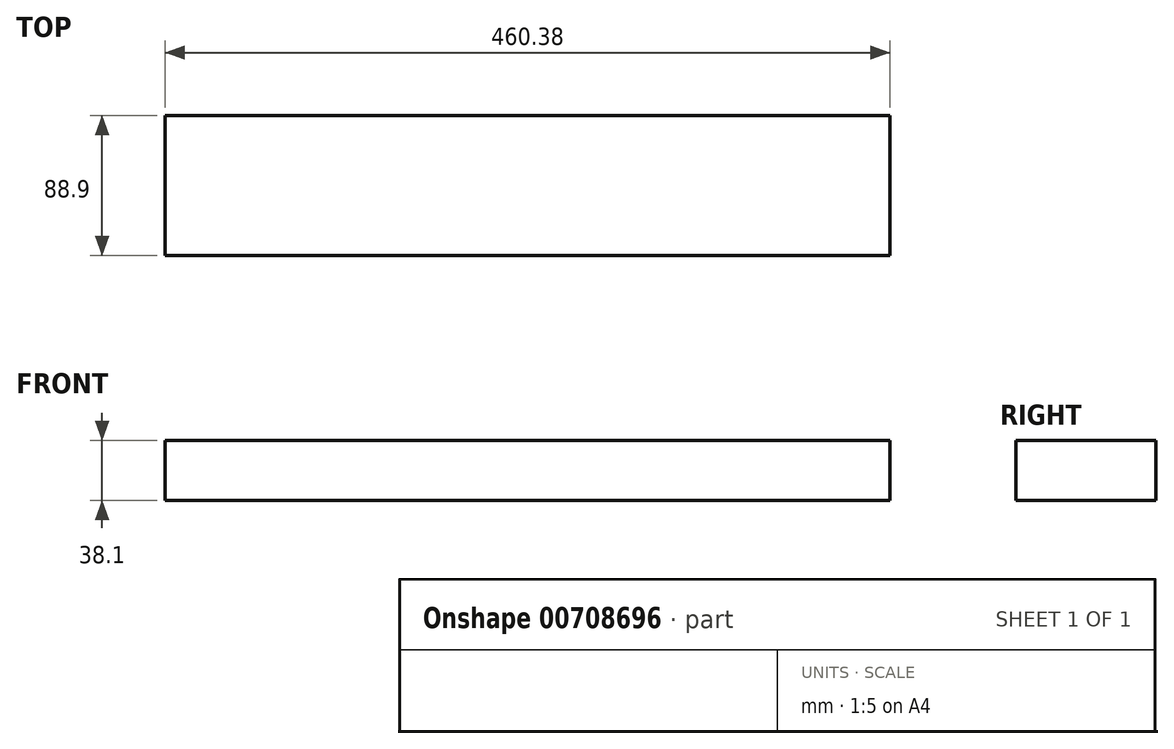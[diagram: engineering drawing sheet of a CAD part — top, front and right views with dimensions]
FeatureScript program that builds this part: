
annotation { "Feature Type Name" : "Feature", "Feature Type Description" : "" }
export const myFeature = defineFeature(function(context is Context, id is Id, definition is map)
    precondition{}
    {
        {
            var Q0;
            Q0=qCreatedBy(makeId("Right.planeOp"),FACE);
            var sketch = newSketch(context, id + "F0", { "sketchPlane" : qUnion([Q0])});
            skLineSegment(sketch, "E0.bottom", {"start": v(44.45, 19.05) * mm, "end": v(-44.45, 19.05) * mm});
            skLineSegment(sketch, "E0.top", {"start": v(44.45, -19.05) * mm, "end": v(-44.45, -19.05) * mm});
            skLineSegment(sketch, "E0.left", {"start": v(44.45, 19.05) * mm, "end": v(44.45, -19.05) * mm});
            skLineSegment(sketch, "E0.right", {"start": v(-44.45, 19.05) * mm, "end": v(-44.45, -19.05) * mm});
            skPoint(sketch, "E0.middle", {"position": v(0, 0) * mm});
            skSolve(sketch);
        }
        {
            var Q0;
            Q0=makeQuery(id+"F0.imprint","IMPRINT",FACE,{"disambiguationData":[TD([[makeQuery(id+"F0.imprint","IMPRINT",EDGE,{"derivedFrom":sQuery(id+"F0.wireOp",EDGE,"E0.bottom")}),1.0]])]});
            extrude(context, id + "F1", {"entities" : qUnion([Q0]), "endBound" : BoundingType.SYMMETRIC, "depth" : 460.38 * mm, "offsetDistance" : 25.4 * mm});
        }
    });
